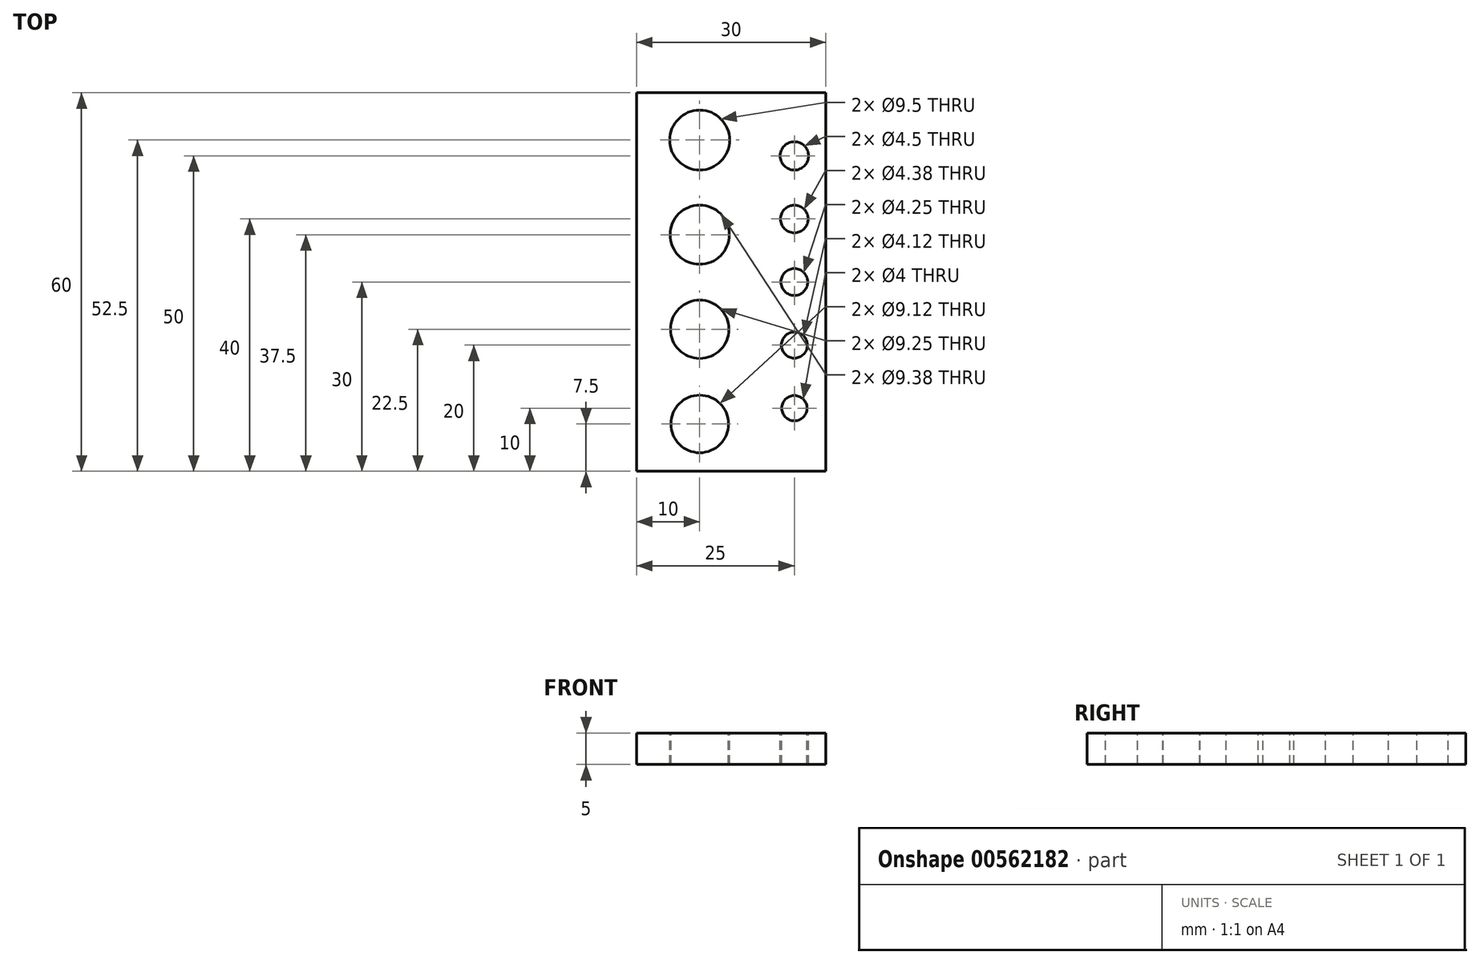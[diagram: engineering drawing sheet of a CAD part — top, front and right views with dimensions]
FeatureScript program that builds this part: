
annotation { "Feature Type Name" : "Feature", "Feature Type Description" : "" }
export const myFeature = defineFeature(function(context is Context, id is Id, definition is map)
    precondition{}
    {
        {
            var Q0;
            Q0=qCreatedBy(makeId("Top.planeOp"),FACE);
            var sketch = newSketch(context, id + "F0", { "sketchPlane" : qUnion([Q0])});
            skLineSegment(sketch, "E0.bottom", {"start": v(-20, 30) * mm, "end": v(10, 30) * mm});
            skLineSegment(sketch, "E0.top", {"start": v(-20, -30) * mm, "end": v(10, -30) * mm});
            skLineSegment(sketch, "E0.left", {"start": v(-20, 30) * mm, "end": v(-20, -30) * mm});
            skLineSegment(sketch, "E0.right", {"start": v(10, 30) * mm, "end": v(10, -30) * mm});
            skSolve(sketch);
        }
        {
            var Q0;
            Q0 = qSketchRegion(id + "F0", true);
            extrude(context, id + "F1", {"entities" : qUnion([Q0]), "depth" : 5 * mm, "offsetDistance" : 25 * mm});
        }
        {
            var Q0;
            Q0=makeQuery(id+"F1.opExtrude","CAP_FACE",FACE,{"disambiguationData":[OSD([sQuery(id+"F0.wireOp",EDGE,"E0.bottom"),sQuery(id+"F0.wireOp",EDGE,"E0.top"),sQuery(id+"F0.wireOp",EDGE,"E0.left"),sQuery(id+"F0.wireOp",EDGE,"E0.right")])],"isStart":false});
            var sketch = newSketch(context, id + "F2", { "sketchPlane" : qUnion([Q0])});
            skCircle(sketch, "E1", {"center": v(-10, 7.5) * mm, "radius": 4.69 * mm});
            skCircle(sketch, "E2", {"center": v(-10, -7.5) * mm, "radius": 4.62 * mm});
            skCircle(sketch, "E3", {"center": v(-10, -22.5) * mm, "radius": 4.56 * mm});
            skCircle(sketch, "E4", {"center": v(-10, 22.5) * mm, "radius": 4.75 * mm});
            skCircle(sketch, "E5", {"center": v(5, -20) * mm, "radius": 2 * mm});
            skCircle(sketch, "E6", {"center": v(5, -10) * mm, "radius": 2.06 * mm});
            skCircle(sketch, "E7", {"center": v(5, 0) * mm, "radius": 2.12 * mm});
            skCircle(sketch, "E8", {"center": v(5, 10) * mm, "radius": 2.19 * mm});
            skCircle(sketch, "E9", {"center": v(5, 20) * mm, "radius": 2.25 * mm});
            skSolve(sketch);
        }
        {
            var Q0;
            Q0=makeQuery(id+"F2.imprint","IMPRINT",FACE,{"disambiguationData":[TD([[makeQuery(id+"F2.imprint","IMPRINT",EDGE,{"derivedFrom":sQuery(id+"F2.wireOp",EDGE,"E4")}),1.0]])]});
            var Q1;
            Q1=makeQuery(id+"F2.imprint","IMPRINT",FACE,{"disambiguationData":[TD([[makeQuery(id+"F2.imprint","IMPRINT",EDGE,{"derivedFrom":sQuery(id+"F2.wireOp",EDGE,"E1")}),1.0]])]});
            var Q2;
            Q2=makeQuery(id+"F2.imprint","IMPRINT",FACE,{"disambiguationData":[TD([[makeQuery(id+"F2.imprint","IMPRINT",EDGE,{"derivedFrom":sQuery(id+"F2.wireOp",EDGE,"E2")}),1.0]])]});
            var Q3;
            Q3=makeQuery(id+"F2.imprint","IMPRINT",FACE,{"disambiguationData":[TD([[makeQuery(id+"F2.imprint","IMPRINT",EDGE,{"derivedFrom":sQuery(id+"F2.wireOp",EDGE,"E3")}),1.0]])]});
            var Q4;
            Q4=makeQuery(id+"F2.imprint","IMPRINT",FACE,{"disambiguationData":[TD([[makeQuery(id+"F2.imprint","IMPRINT",EDGE,{"derivedFrom":sQuery(id+"F2.wireOp",EDGE,"E5")}),1.0]])]});
            var Q5;
            Q5=makeQuery(id+"F2.imprint","IMPRINT",FACE,{"disambiguationData":[TD([[makeQuery(id+"F2.imprint","IMPRINT",EDGE,{"derivedFrom":sQuery(id+"F2.wireOp",EDGE,"E6")}),1.0]])]});
            var Q6;
            Q6=makeQuery(id+"F2.imprint","IMPRINT",FACE,{"disambiguationData":[TD([[makeQuery(id+"F2.imprint","IMPRINT",EDGE,{"derivedFrom":sQuery(id+"F2.wireOp",EDGE,"E7")}),1.0]])]});
            var Q7;
            Q7=makeQuery(id+"F2.imprint","IMPRINT",FACE,{"disambiguationData":[TD([[makeQuery(id+"F2.imprint","IMPRINT",EDGE,{"derivedFrom":sQuery(id+"F2.wireOp",EDGE,"E8")}),1.0]])]});
            var Q8;
            Q8=makeQuery(id+"F2.imprint","IMPRINT",FACE,{"disambiguationData":[TD([[makeQuery(id+"F2.imprint","IMPRINT",EDGE,{"derivedFrom":sQuery(id+"F2.wireOp",EDGE,"E9")}),1.0]])]});
            extrude(context, id + "F3", {"entities" : qUnion([Q0, Q1, Q2, Q3, Q4, Q5, Q6, Q7, Q8]), "operationType" : NewBodyOperationType.REMOVE, "endBound" : BoundingType.THROUGH_ALL, "oppositeDirection" : true, "depth" : 25 * mm, "offsetDistance" : 25 * mm});
        }
    });
